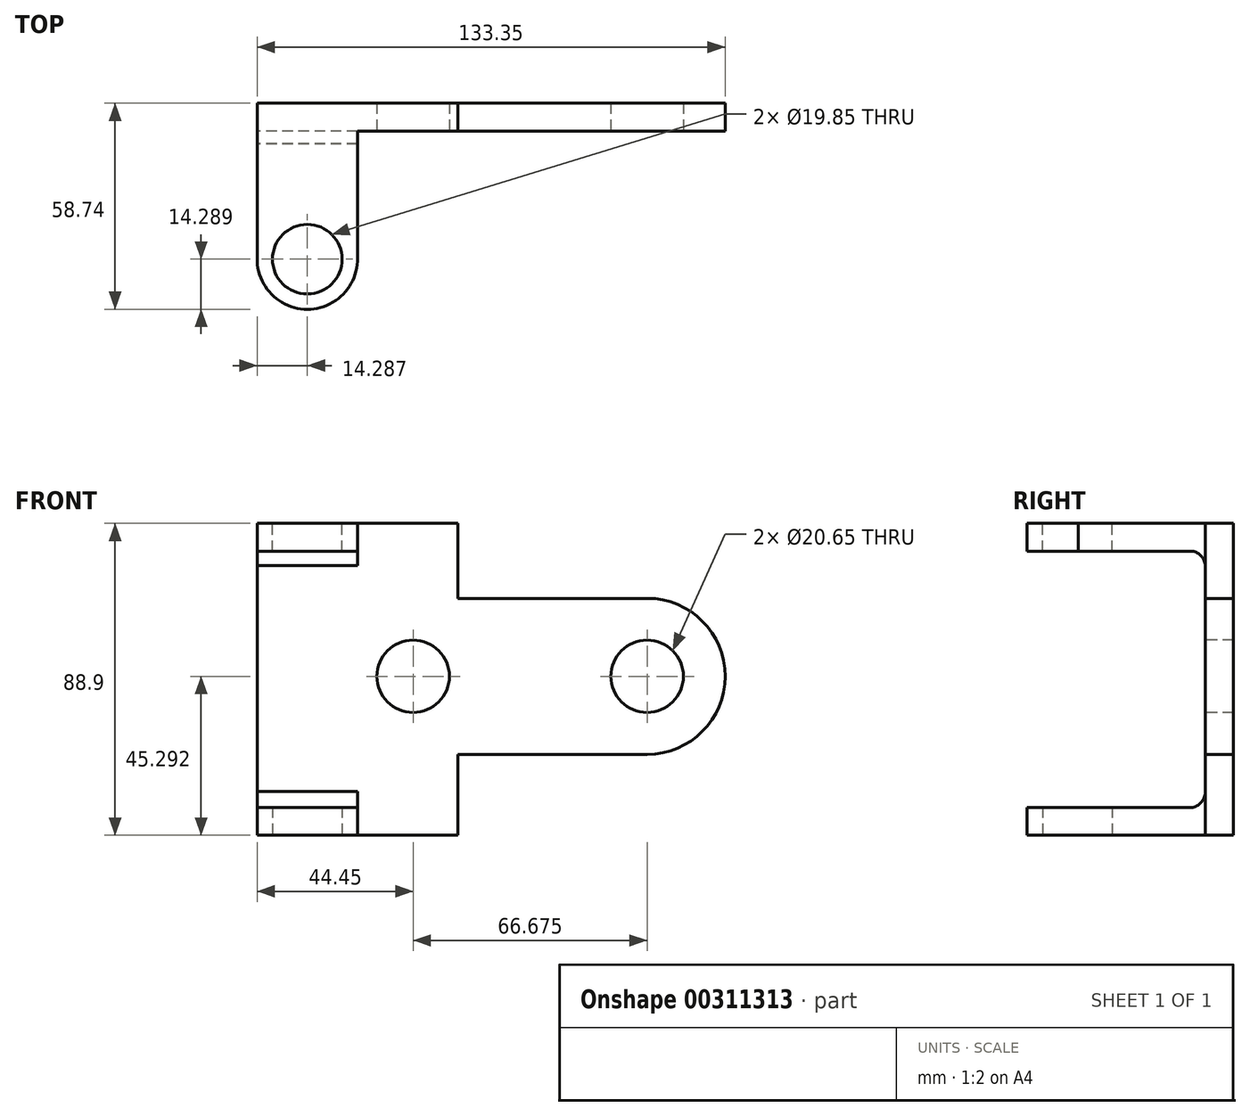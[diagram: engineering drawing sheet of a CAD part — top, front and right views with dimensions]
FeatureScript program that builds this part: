
annotation { "Feature Type Name" : "Feature", "Feature Type Description" : "" }
export const myFeature = defineFeature(function(context is Context, id is Id, definition is map)
    precondition{}
    {
        {
            var Q0;
            Q0=qCreatedBy(makeId("Front.planeOp"),FACE);
            var sketch = newSketch(context, id + "F0", { "sketchPlane" : qUnion([Q0])});
            skLineSegment(sketch, "E0", {"start": v(0, 0) * mm, "end": v(0, 88.9) * mm});
            skLineSegment(sketch, "E1", {"start": v(0, 88.9) * mm, "end": v(57.15, 88.9) * mm});
            skLineSegment(sketch, "E2", {"start": v(57.15, 88.9) * mm, "end": v(57.15, 0) * mm});
            skLineSegment(sketch, "E3", {"start": v(57.15, 0) * mm, "end": v(0, 0) * mm});
            skSolve(sketch);
        }
        {
            var Q0;
            Q0 = qSketchRegion(id + "F0", true);
            extrude(context, id + "F1", {"entities" : qUnion([Q0]), "endBound" : BoundingType.SYMMETRIC, "depth" : 7.94 * mm});
        }
        {
            var Q0;
            Q0=makeQuery(id+"F1.opExtrude","SWEPT_FACE",FACE,{"disambiguationData":[OSD([sQuery(id+"F0.wireOp",EDGE,"E3")])]});
            var sketch = newSketch(context, id + "F2", { "sketchPlane" : qUnion([Q0])});
            skLineSegment(sketch, "E4", {"start": v(0, -3.97) * mm, "end": v(0, 40.48) * mm});
            skLineSegment(sketch, "E5", {"start": v(28.57, 40.48) * mm, "end": v(28.58, -3.97) * mm});
            skLineSegment(sketch, "E6", {"start": v(28.58, -3.97) * mm, "end": v(0, -3.97) * mm});
            skArc(sketch, "E7", {"start": v(28.58, 40.48) * mm, "mid": v(14.29, 54.77) * mm, "end": v(0, 40.48) * mm});
            skSolve(sketch);
        }
        {
            var Q0;
            Q0 = qSketchRegion(id + "F2", true);
            extrude(context, id + "F3", {"entities" : qUnion([Q0]), "operationType" : NewBodyOperationType.ADD, "oppositeDirection" : true, "depth" : 7.94 * mm});
        }
        {
            var Q0;
            Q0=makeQuery(id+"F1.opExtrude","SWEPT_FACE",FACE,{"disambiguationData":[OSD([sQuery(id+"F0.wireOp",EDGE,"E1")])]});
            var sketch = newSketch(context, id + "F4", { "sketchPlane" : qUnion([Q0])});
            skLineSegment(sketch, "E8", {"start": v(28.57, 3.97) * mm, "end": v(28.57, -40.48) * mm});
            skLineSegment(sketch, "E9", {"start": v(0, -40.48) * mm, "end": v(0, 3.97) * mm});
            skLineSegment(sketch, "E10", {"start": v(0, 3.97) * mm, "end": v(28.57, 3.97) * mm});
            skArc(sketch, "E11", {"start": v(0, -40.16) * mm, "mid": v(14.29, -54.77) * mm, "end": v(28.58, -40.16) * mm});
            skSolve(sketch);
        }
        {
            var Q0;
            Q0 = qSketchRegion(id + "F4", true);
            extrude(context, id + "F5", {"entities" : qUnion([Q0]), "operationType" : NewBodyOperationType.ADD, "oppositeDirection" : true, "depth" : 7.94 * mm});
        }
        {
            var Q0;
            Q0=makeQuery(id+"F5.boolean.opBoolean","MERGE",FACE,{"derivedFrom":[makeQuery(id+"F3.boolean.opBoolean","MERGE",FACE,{"derivedFrom":[makeQuery(id+"F1.opExtrude","SWEPT_FACE",FACE,{"disambiguationData":[OSD([sQuery(id+"F0.wireOp",EDGE,"E0")])]}),makeQuery(id+"F3.opExtrude","SWEPT_FACE",FACE,{"disambiguationData":[OSD([sQuery(id+"F2.wireOp",EDGE,"E4")])]})]}),makeQuery(id+"F5.opExtrude","SWEPT_FACE",FACE,{"disambiguationData":[OSD([sQuery(id+"F4.wireOp",EDGE,"E9")])]})]});
            var sketch = newSketch(context, id + "F6", { "sketchPlane" : qUnion([Q0])});
            skArc(sketch, "E12", {"start": v(9.7, 80.96) * mm, "mid": v(5.94, 80.2) * mm, "end": v(3.97, 76.9) * mm});
            skArc(sketch, "E13", {"start": v(3.97, 12.46) * mm, "mid": v(5.85, 8.76) * mm, "end": v(9.92, 7.94) * mm});
            skLineSegment(sketch, "E14", {"start": v(9.7, 80.96) * mm, "end": v(3.97, 80.96) * mm});
            skLineSegment(sketch, "E15", {"start": v(3.97, 80.96) * mm, "end": v(3.97, 76.9) * mm});
            skLineSegment(sketch, "E16", {"start": v(9.92, 7.94) * mm, "end": v(3.97, 7.94) * mm});
            skLineSegment(sketch, "E17", {"start": v(3.97, 7.94) * mm, "end": v(3.97, 12.46) * mm});
            skSolve(sketch);
        }
        {
            var Q0;
            Q0 = qSketchRegion(id + "F6", true);
            extrude(context, id + "F7", {"entities" : qUnion([Q0]), "operationType" : NewBodyOperationType.ADD, "oppositeDirection" : true, "depth" : 28.57 * mm});
        }
        {
            var Q0;
            Q0=makeQuery(id+"F3.boolean.opBoolean","MERGE",FACE,{"derivedFrom":[makeQuery(id+"F1.opExtrude","SWEPT_FACE",FACE,{"disambiguationData":[OSD([sQuery(id+"F0.wireOp",EDGE,"E3")])]}),makeQuery(id+"F3.opExtrude","CAP_FACE",FACE,{"disambiguationData":[OSD([sQuery(id+"F2.wireOp",EDGE,"E4"),sQuery(id+"F2.wireOp",EDGE,"E5"),sQuery(id+"F2.wireOp",EDGE,"E6"),sQuery(id+"F2.wireOp",EDGE,"E7")])],"isStart":true})]});
            var sketch = newSketch(context, id + "F8", { "sketchPlane" : qUnion([Q0])});
            skCircle(sketch, "E18", {"center": v(14.29, 40.48) * mm, "radius": 9.92 * mm});
            skSolve(sketch);
        }
        {
            var Q0;
            Q0 = qSketchRegion(id + "F8", true);
            extrude(context, id + "F9", {"entities" : qUnion([Q0]), "operationType" : NewBodyOperationType.REMOVE, "oppositeDirection" : true, "depth" : 25.4 * mm});
        }
        {
            var Q0;
            Q0=makeQuery(id+"F5.boolean.opBoolean","MERGE",FACE,{"derivedFrom":[makeQuery(id+"F1.opExtrude","SWEPT_FACE",FACE,{"disambiguationData":[OSD([sQuery(id+"F0.wireOp",EDGE,"E1")])]}),makeQuery(id+"F5.opExtrude","CAP_FACE",FACE,{"disambiguationData":[OSD([sQuery(id+"F4.wireOp",EDGE,"E8"),sQuery(id+"F4.wireOp",EDGE,"E9"),sQuery(id+"F4.wireOp",EDGE,"E10"),sQuery(id+"F4.wireOp",EDGE,"E11")])],"isStart":true})]});
            var sketch = newSketch(context, id + "F10", { "sketchPlane" : qUnion([Q0])});
            skCircle(sketch, "E19", {"center": v(14.29, -40.48) * mm, "radius": 9.92 * mm});
            skSolve(sketch);
        }
        {
            var Q0;
            Q0 = qSketchRegion(id + "F10", true);
            extrude(context, id + "F11", {"entities" : qUnion([Q0]), "operationType" : NewBodyOperationType.REMOVE, "oppositeDirection" : true, "depth" : 25.4 * mm});
        }
        {
            var Q0;
            Q0=makeQuery(id+"F1.opExtrude","CAP_FACE",FACE,{"disambiguationData":[OSD([sQuery(id+"F0.wireOp",EDGE,"E0"),sQuery(id+"F0.wireOp",EDGE,"E1"),sQuery(id+"F0.wireOp",EDGE,"E2"),sQuery(id+"F0.wireOp",EDGE,"E3")])],"isStart":true});
            var sketch = newSketch(context, id + "F12", { "sketchPlane" : qUnion([Q0])});
            skPoint(sketch, "E20.end.orphan", {"position": v(-57.15, 44.45) * mm});
            skPoint(sketch, "E20.start.orphan", {"position": v(0, 44.45) * mm});
            skLineSegment(sketch, "E21", {"start": v(-111.12, 67.52) * mm, "end": v(-57.15, 67.52) * mm});
            skLineSegment(sketch, "E22", {"start": v(-111.12, 23.07) * mm, "end": v(-57.15, 23.07) * mm});
            skArc(sketch, "E23", {"start": v(-111.12, 67.52) * mm, "mid": v(-133.35, 45.3) * mm, "end": v(-111.12, 23.07) * mm});
            skLineSegment(sketch, "E24", {"start": v(-57.15, 67.52) * mm, "end": v(-57.15, 23.07) * mm});
            skSolve(sketch);
        }
        {
            var Q0;
            Q0 = qSketchRegion(id + "F12", true);
            extrude(context, id + "F13", {"entities" : qUnion([Q0]), "operationType" : NewBodyOperationType.ADD, "oppositeDirection" : true, "depth" : 7.94 * mm});
        }
        {
            var Q0;
            Q0=makeQuery(id+"F13.boolean.opBoolean","MERGE",FACE,{"derivedFrom":[makeQuery(id+"F1.opExtrude","CAP_FACE",FACE,{"disambiguationData":[OSD([sQuery(id+"F0.wireOp",EDGE,"E0"),sQuery(id+"F0.wireOp",EDGE,"E1"),sQuery(id+"F0.wireOp",EDGE,"E2"),sQuery(id+"F0.wireOp",EDGE,"E3")])],"isStart":false}),makeQuery(id+"F13.opExtrude","CAP_FACE",FACE,{"disambiguationData":[OSD([sQuery(id+"F12.wireOp",EDGE,"E21"),sQuery(id+"F12.wireOp",EDGE,"E22"),sQuery(id+"F12.wireOp",EDGE,"E23"),sQuery(id+"F12.wireOp",EDGE,"E24")])],"isStart":false})]});
            var sketch = newSketch(context, id + "F14", { "sketchPlane" : qUnion([Q0])});
            skCircle(sketch, "E25", {"center": v(111.12, 45.3) * mm, "radius": 10.33 * mm});
            skCircle(sketch, "E26", {"center": v(44.45, 45.3) * mm, "radius": 10.33 * mm});
            skSolve(sketch);
        }
        {
            var Q0;
            Q0 = qSketchRegion(id + "F14", true);
            extrude(context, id + "F15", {"entities" : qUnion([Q0]), "operationType" : NewBodyOperationType.REMOVE, "oppositeDirection" : true, "depth" : 25.4 * mm});
        }
        {
            var Q0;
            Q0 = qSketchRegion(id + "F14", true);
            extrude(context, id + "F16", {"entities" : qUnion([Q0]), "operationType" : NewBodyOperationType.REMOVE, "oppositeDirection" : true, "depth" : 25.4 * mm});
        }
        {
            var Q0;
            Q0=makeQuery(id+"F13.boolean.opBoolean","MERGE",FACE,{"derivedFrom":[makeQuery(id+"F1.opExtrude","CAP_FACE",FACE,{"disambiguationData":[OSD([sQuery(id+"F0.wireOp",EDGE,"E0"),sQuery(id+"F0.wireOp",EDGE,"E1"),sQuery(id+"F0.wireOp",EDGE,"E2"),sQuery(id+"F0.wireOp",EDGE,"E3")])],"isStart":false}),makeQuery(id+"F13.opExtrude","CAP_FACE",FACE,{"disambiguationData":[OSD([sQuery(id+"F12.wireOp",EDGE,"E21"),sQuery(id+"F12.wireOp",EDGE,"E22"),sQuery(id+"F12.wireOp",EDGE,"E23"),sQuery(id+"F12.wireOp",EDGE,"E24")])],"isStart":false})]});
            var sketch = newSketch(context, id + "F17", { "sketchPlane" : qUnion([Q0])});
            skArc(sketch, "E27", {"start": v(57.15, 78.2) * mm, "mid": v(47.69, 76.67) * mm, "end": v(50.53, 67.52) * mm});
            skArc(sketch, "E28", {"start": v(51.94, 23.07) * mm, "mid": v(48.28, 14.47) * mm, "end": v(57.15, 11.53) * mm});
            skLineSegment(sketch, "E29", {"start": v(57.15, 67.52) * mm, "end": v(50.53, 67.52) * mm});
            skLineSegment(sketch, "E30", {"start": v(57.15, 67.52) * mm, "end": v(57.15, 78.2) * mm});
            skLineSegment(sketch, "E31", {"start": v(57.15, 23.07) * mm, "end": v(51.94, 23.07) * mm});
            skLineSegment(sketch, "E32", {"start": v(57.15, 23.07) * mm, "end": v(57.15, 11.53) * mm});
            skSolve(sketch);
        }
        {
            var Q0;
            Q0 = qSketchRegion(id + "F17", true);
            extrude(context, id + "F18", {"entities" : qUnion([Q0]), "operationType" : NewBodyOperationType.ADD, "oppositeDirection" : true, "depth" : 7.94 * mm});
        }
    });
